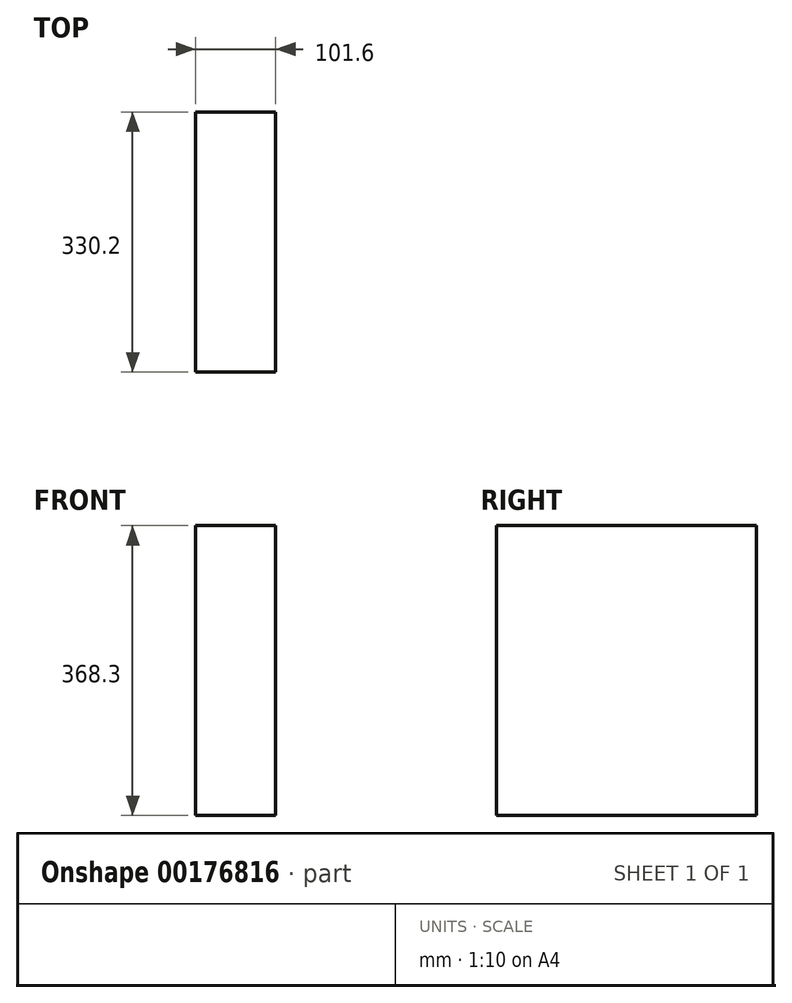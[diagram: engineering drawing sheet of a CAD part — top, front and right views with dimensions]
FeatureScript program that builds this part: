
annotation { "Feature Type Name" : "Feature", "Feature Type Description" : "" }
export const myFeature = defineFeature(function(context is Context, id is Id, definition is map)
    precondition{}
    {
        {
            var Q0;
            Q0=qCreatedBy(makeId("Top.planeOp"),FACE);
            var sketch = newSketch(context, id + "F0", { "sketchPlane" : qUnion([Q0])});
            skLineSegment(sketch, "E0.bottom", {"start": v(50.8, 165.1) * mm, "end": v(-50.8, 165.1) * mm});
            skLineSegment(sketch, "E0.top", {"start": v(50.8, -165.1) * mm, "end": v(-50.8, -165.1) * mm});
            skLineSegment(sketch, "E0.left", {"start": v(50.8, 165.1) * mm, "end": v(50.8, -165.1) * mm});
            skLineSegment(sketch, "E0.right", {"start": v(-50.8, 165.1) * mm, "end": v(-50.8, -165.1) * mm});
            skPoint(sketch, "E0.middle", {"position": v(0, 0) * mm});
            skSolve(sketch);
        }
        {
            var Q0;
            Q0 = qSketchRegion(id + "F0", true);
            extrude(context, id + "F1", {"entities" : qUnion([Q0]), "depth" : 368.3 * mm});
        }
    });
